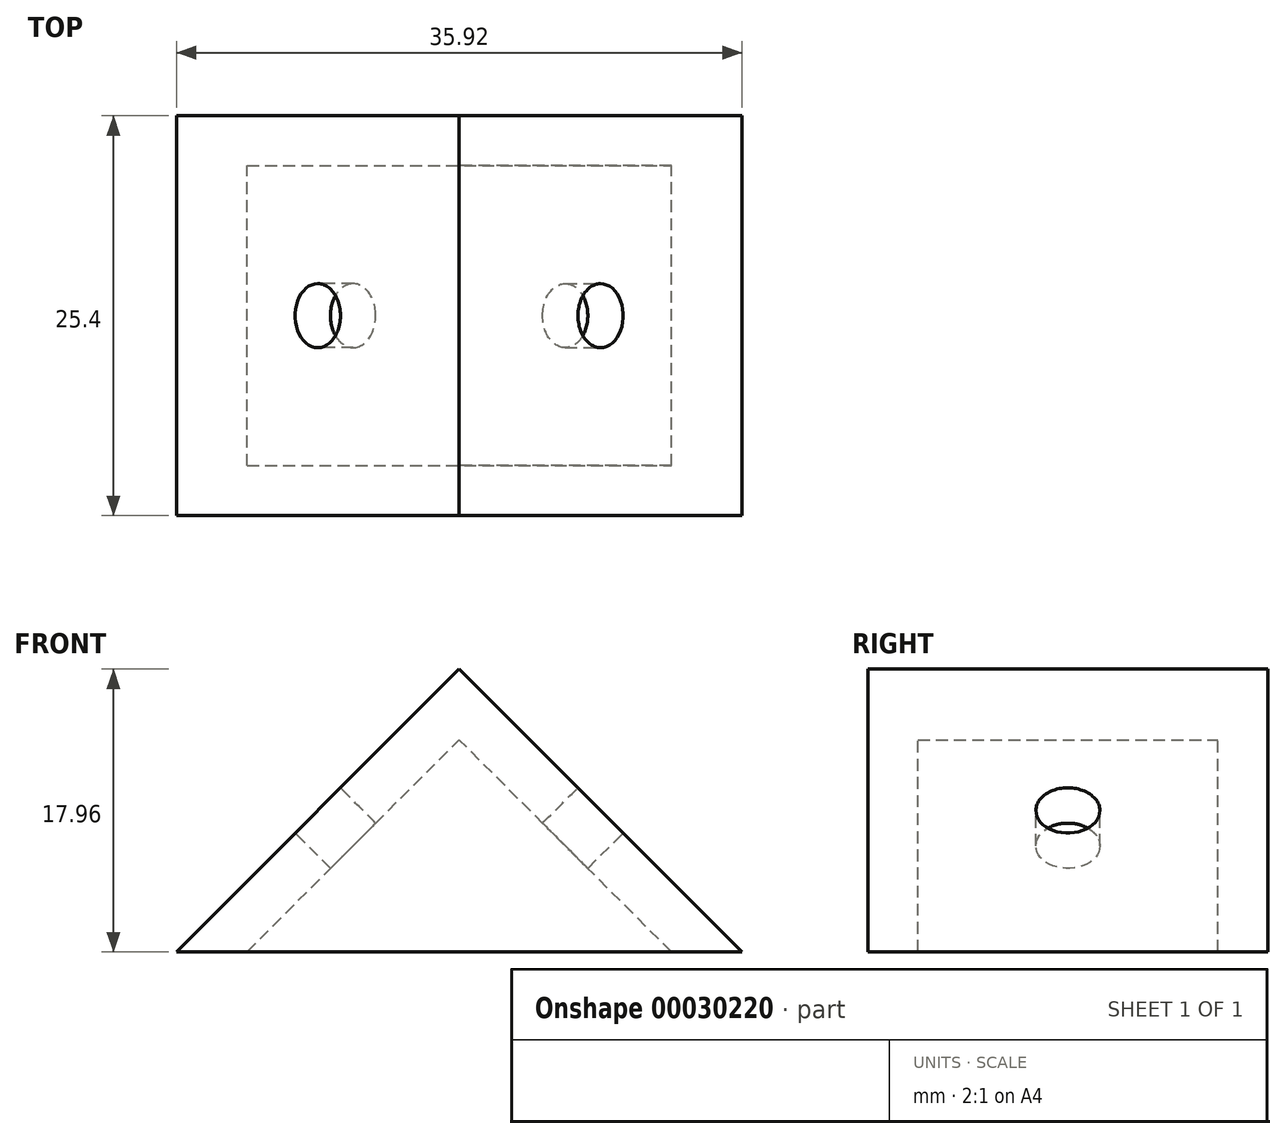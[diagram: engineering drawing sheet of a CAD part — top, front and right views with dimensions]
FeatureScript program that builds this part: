
annotation { "Feature Type Name" : "Feature", "Feature Type Description" : "" }
export const myFeature = defineFeature(function(context is Context, id is Id, definition is map)
    precondition{}
    {
        {
            var Q0;
            Q0=qCreatedBy(makeId("Front.planeOp"),FACE);
            var sketch = newSketch(context, id + "F0", { "sketchPlane" : qUnion([Q0])});
            skLineSegment(sketch, "E0", {"start": v(0, 17.96) * mm, "end": v(-17.96, 0) * mm});
            skLineSegment(sketch, "E1", {"start": v(-17.96, 0) * mm, "end": v(-13.47, 0) * mm});
            skLineSegment(sketch, "E2", {"start": v(-13.47, 0) * mm, "end": v(0, 13.47) * mm});
            skLineSegment(sketch, "E3", {"start": v(0, 17.96) * mm, "end": v(0, 13.47) * mm});
            skSolve(sketch);
        }
        {
            var Q0;
            Q0=makeQuery(id+"F0.imprint","IMPRINT",FACE,{"disambiguationData":[TD([[makeQuery(id+"F0.imprint","IMPRINT",EDGE,{"derivedFrom":sQuery(id+"F0.wireOp",EDGE,"E0")}),1.0]])]});
            extrude(context, id + "F1", {"entities" : qUnion([Q0]), "depth" : 12.7 * mm});
        }
        {
            var Q0;
            Q0=makeQuery(id+"F1.opExtrude","CAP_FACE",FACE,{"disambiguationData":[OSD([sQuery(id+"F0.wireOp",EDGE,"E0"),sQuery(id+"F0.wireOp",EDGE,"E1"),sQuery(id+"F0.wireOp",EDGE,"E2"),sQuery(id+"F0.wireOp",EDGE,"E3")])],"isStart":false});
            var sketch = newSketch(context, id + "F2", { "sketchPlane" : qUnion([Q0])});
            skLineSegment(sketch, "E4", {"start": v(0, 13.47) * mm, "end": v(-13.47, 0) * mm});
            skLineSegment(sketch, "E5", {"start": v(-13.47, 0) * mm, "end": v(0, 0) * mm});
            skLineSegment(sketch, "E6", {"start": v(0, 0) * mm, "end": v(0, 13.47) * mm});
            skSolve(sketch);
        }
        {
            var Q0;
            Q0=makeQuery(id+"F2.imprint","IMPRINT",FACE,{"disambiguationData":[TD([[makeQuery(id+"F2.imprint","IMPRINT",EDGE,{"derivedFrom":sQuery(id+"F2.wireOp",EDGE,"E4")}),-1.0]])]});
            extrude(context, id + "F3", {"entities" : qUnion([Q0]), "operationType" : NewBodyOperationType.ADD, "oppositeDirection" : true, "depth" : 3.17 * mm});
        }
        {
            var Q0;
            Q0=makeQuery(id+"F1.opExtrude","SWEPT_FACE",FACE,{"disambiguationData":[OSD([sQuery(id+"F0.wireOp",EDGE,"E0")])]});
            var sketch = newSketch(context, id + "F4", { "sketchPlane" : qUnion([Q0])});
            skCircle(sketch, "E7", {"center": v(0, 0) * mm, "radius": 2.03 * mm});
            skSolve(sketch);
        }
        {
            var Q0;
            Q0 = qSketchRegion(id + "F4", true);
            extrude(context, id + "F5", {"entities" : qUnion([Q0]), "operationType" : NewBodyOperationType.REMOVE, "endBound" : BoundingType.THROUGH_ALL, "oppositeDirection" : true, "depth" : 25.4 * mm});
        }
        {
            var Q0;
            Q0=makeQuery(id+"F1.opExtrude","SWEPT_BODY",BODY,{"disambiguationData":[OSD([sQuery(id+"F0.wireOp",EDGE,"E0"),sQuery(id+"F0.wireOp",EDGE,"E1"),sQuery(id+"F0.wireOp",EDGE,"E2"),sQuery(id+"F0.wireOp",EDGE,"E3")])]});
            var Q1;
            Q1=makeQuery(id+"F3.boolean.opBoolean","MERGE",FACE,{"derivedFrom":[makeQuery(id+"F1.opExtrude","SWEPT_FACE",FACE,{"disambiguationData":[OSD([sQuery(id+"F0.wireOp",EDGE,"E3")])]}),makeQuery(id+"F3.opExtrude","SWEPT_FACE",FACE,{"disambiguationData":[OSD([sQuery(id+"F2.wireOp",EDGE,"E6")])]})]});
            mirror(context, id + "F6", {"operationType" : NewBodyOperationType.ADD, "entities" : qUnion([Q0]), "mirrorPlane" : qUnion([Q1])});
        }
        {
            var Q0;
            Q0=makeQuery(id+"F1.opExtrude","SWEPT_BODY",BODY,{"disambiguationData":[OSD([sQuery(id+"F0.wireOp",EDGE,"E0"),sQuery(id+"F0.wireOp",EDGE,"E1"),sQuery(id+"F0.wireOp",EDGE,"E2"),sQuery(id+"F0.wireOp",EDGE,"E3")])]});
            var Q1;
            {var subQ0=sQuery(id+"F0.wireOp",EDGE,"E0");var subQ1=sQuery(id+"F0.wireOp",EDGE,"E2");var subQ2=sQuery(id+"F0.wireOp",EDGE,"E3");var subQ3=makeQuery(id+"F5.boolean.opBoolean","SPLIT",FACE,{"disambiguationData":[TD([makeQuery(id+"F1.opExtrude","SWEPT_FACE",FACE,{"disambiguationData":[OSD([subQ2])]})])],"derivedFrom":makeQuery(id+"F1.opExtrude","CAP_FACE",FACE,{"disambiguationData":[OSD([subQ0,sQuery(id+"F0.wireOp",EDGE,"E1"),subQ1,subQ2])],"isStart":true})});Q1=makeQuery(id+"F6.boolean.opBoolean","MERGE",FACE,{"derivedFrom":[subQ3,makeQuery(id+"F6.opPattern","COPY",FACE,{"derivedFrom":subQ3,"instanceName":"1"})]});}
            mirror(context, id + "F7", {"operationType" : NewBodyOperationType.ADD, "entities" : qUnion([Q0]), "mirrorPlane" : qUnion([Q1])});
        }
    });
